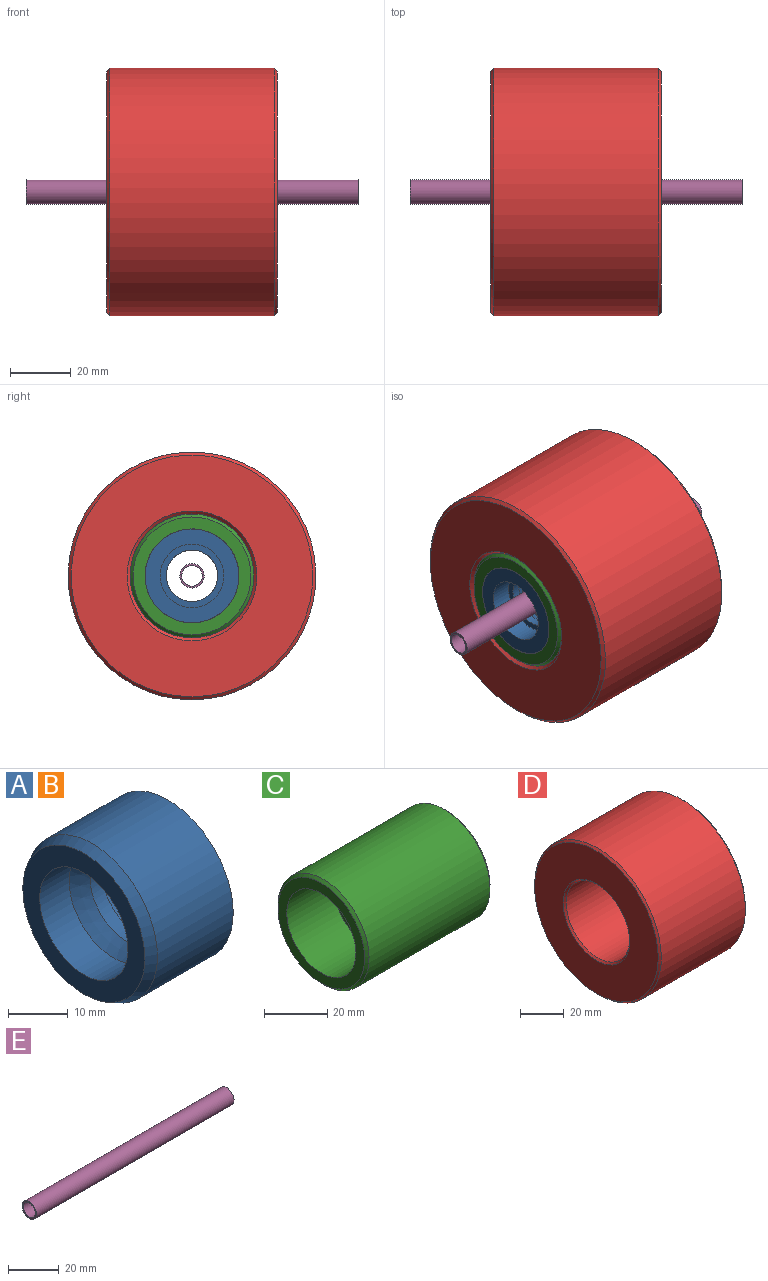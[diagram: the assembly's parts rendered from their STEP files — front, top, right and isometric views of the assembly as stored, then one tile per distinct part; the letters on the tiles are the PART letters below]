
ASSEMBLY  parts=5 mates=8
PART A: 9 faces, bbox 20x31x31 mm
  f0: cylinder r=8.5mm len=17mm, axis (1,0,0), area 149.5mm2, adj f6,f8
  f1: cylinder r=15.5mm len=31mm, axis (-1,0,0), area 1753mm2, adj f2,f4
  f2: plane 31x31mm, normal (1,0,0), area 408.4mm2, adj f1,f5
  f3: plane 29x29mm, normal (-1,0,0), area 314.2mm2, adj f4,f7
  f4: cone r=15.5mm half-angle=26.6deg, axis (1,0,0), area 210.7mm2, adj f1,f3
  f5: cylinder r=10.5mm len=21mm, axis (1,0,0), area 475mm2, adj f2,f6
  f6: plane 21x21mm, normal (1,0,0), area 119.4mm2, adj f0,f5
  f7: cylinder r=10.5mm len=21mm, axis (-1,0,0), area 461.8mm2, adj f3,f8
  f8: cone r=10.5mm half-angle=33.7deg, axis (-1,0,0), area 215.2mm2, adj f0,f7
PART B: same geometry as A
PART C: 10 faces, bbox 56.3x40.9x40.9 mm
  f0: cylinder r=12.83mm len=25.66mm, axis (1,0,0), area 1232.6mm2, adj f4,f6
  f1: cylinder r=20.45mm len=54.29mm, axis (-1,0,0), area 6974.1mm2, adj f8,f9
  f2: plane 38.89x38.89mm, normal (1,0,0), area 433.1mm2, adj f5,f8
  f3: plane 38.89x38.89mm, normal (-1,0,0), area 433.1mm2, adj f7,f9
  f4: plane 31x31mm, normal (1,0,0), area 237.6mm2, adj f0,f5
  f5: cylinder r=15.5mm len=31mm, axis (1,0,0), area 1947.8mm2, adj f2,f4
  f6: plane 31x31mm, normal (-1,0,0), area 237.6mm2, adj f0,f7
  f7: cylinder r=15.5mm len=31mm, axis (-1,0,0), area 2045.2mm2, adj f3,f6
  f8: cone r=19.45mm half-angle=45deg, axis (-1,0,0), area 177.2mm2, adj f1,f2
  f9: cone r=20.45mm half-angle=45deg, axis (1,0,0), area 177.2mm2, adj f1,f3
PART D: 8 faces, bbox 56.3x81.8x81.8 mm
  f0: cylinder r=40.88mm len=81.77mm, axis (-1,0,0), area 13946.5mm2, adj f6,f7
  f1: plane 79.77x79.77mm, normal (1,0,0), area 3552.9mm2, adj f4,f6
  f2: plane 79.77x79.77mm, normal (-1,0,0), area 3552.9mm2, adj f5,f7
  f3: cylinder r=20.45mm len=54.29mm, axis (1,0,0), area 6974.1mm2, adj f4,f5
  f4: cone r=20.45mm half-angle=45deg, axis (1,0,0), area 186.1mm2, adj f1,f3
  f5: cone r=21.45mm half-angle=45deg, axis (-1,0,0), area 186.1mm2, adj f2,f3
  f6: cone r=39.88mm half-angle=45deg, axis (-1,0,0), area 358.9mm2, adj f0,f1
  f7: cone r=40.88mm half-angle=45deg, axis (1,0,0), area 358.9mm2, adj f0,f2
PART E: 4 faces, bbox 109.6x8x8 mm
  f0: cylinder r=4mm len=109.59mm, axis (-1,0,0), area 2754.3mm2, adj f1,f2
  f1: plane 8x8mm, normal (1,0,0), area 14.2mm2, adj f0,f3
  f2: plane 8x8mm, normal (-1,0,0), area 14.2mm2, adj f0,f3
  f3: cylinder r=3.39mm len=109.59mm, axis (1,0,0), area 2334.3mm2, adj f1,f2
PLACE A rot(axis=(0,1,0),180deg) t=(-18.22,0.03,0.11)mm
PLACE B rot(axis=(1,0,0),90deg) t=(18.07,0.03,0.11)mm
PLACE C rot(axis=(-1,0,0),4deg) t=(-0.08,0.03,0.11)mm
PLACE D rot(axis=(1,0,0),0deg) t=(-0.08,0.03,0.11)mm
PLACE E t=(-2.48,0.03,0.11)mm fixed
MATE planar E.f3 <-> D.f0  axis (1,0,0) through (-0.08,0.03,0.11)mm
MATE planar B.f0 <-> C.f0  axis (1,0,0) through (28.07,0.03,0.11)mm
MATE planar C.f5 <-> A.f0  axis (-1,0,0) through (-28.22,0.03,0.11)mm
MATE cylindrical A.f1 <-> E.f0  axis (1,0,0) through (-10.22,0.03,0.11)mm
MATE planar C.f0 <-> D.f0  axis (1,0,0) through (28.07,0.03,0.11)mm
MATE cylindrical B.f1 <-> E.f0  axis (-1,0,0) through (19.07,0.03,0.11)mm
MATE cylindrical D.f0 <-> C.f1  axis (-1,0,0) through (-0.08,0.03,0.11)mm
MATE cylindrical C.f1 <-> E.f0  axis (-1,0,0) through (-27.22,0.03,0.11)mm
